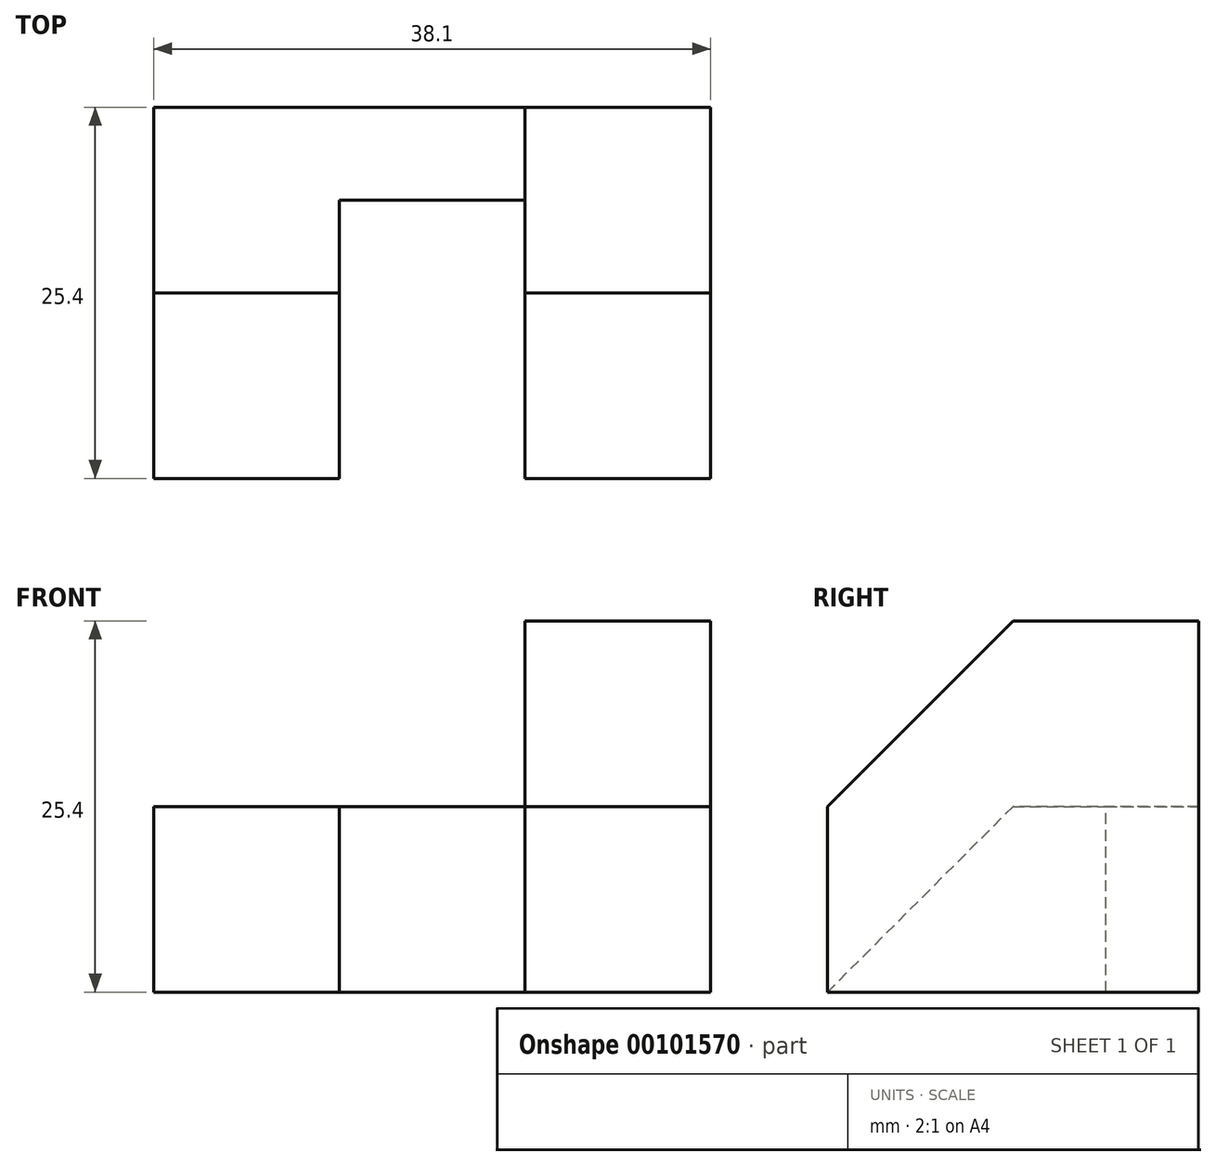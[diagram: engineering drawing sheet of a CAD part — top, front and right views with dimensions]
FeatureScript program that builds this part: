
annotation { "Feature Type Name" : "Feature", "Feature Type Description" : "" }
export const myFeature = defineFeature(function(context is Context, id is Id, definition is map)
    precondition{}
    {
        {
            var Q0;
            Q0=qCreatedBy(makeId("Right.planeOp"),FACE);
            var sketch = newSketch(context, id + "F0", { "sketchPlane" : qUnion([Q0])});
            skLineSegment(sketch, "E0.bottom", {"start": v(0, 0) * mm, "end": v(-25.4, 0) * mm});
            skLineSegment(sketch, "E0.top", {"start": v(0, -25.4) * mm, "end": v(-25.4, -25.4) * mm});
            skLineSegment(sketch, "E0.left", {"start": v(0, 0) * mm, "end": v(0, -25.4) * mm});
            skLineSegment(sketch, "E0.right", {"start": v(-25.4, 0) * mm, "end": v(-25.4, -25.4) * mm});
            skSolve(sketch);
        }
        {
            var Q0;
            Q0 = qSketchRegion(id + "F0", true);
            extrude(context, id + "F1", {"entities" : qUnion([Q0]), "endBound" : BoundingType.SYMMETRIC, "oppositeDirection" : true, "depth" : 38.1 * mm});
        }
        {
            var Q0;
            Q0=qCreatedBy(makeId("Top.planeOp"),FACE);
            var sketch = newSketch(context, id + "F2", { "sketchPlane" : qUnion([Q0])});
            skLineSegment(sketch, "E1.bottom", {"start": v(6.35, -25.4) * mm, "end": v(-6.35, -25.4) * mm});
            skLineSegment(sketch, "E1.top", {"start": v(6.35, -6.35) * mm, "end": v(-6.35, -6.35) * mm});
            skLineSegment(sketch, "E1.left", {"start": v(6.35, -25.4) * mm, "end": v(6.35, -6.35) * mm});
            skLineSegment(sketch, "E1.right", {"start": v(-6.35, -25.4) * mm, "end": v(-6.35, -6.35) * mm});
            skLineSegment(sketch, "E2", {"start": v(0, 0) * mm, "end": v(0, -25.4) * mm, "construction": true});
            skSolve(sketch);
        }
        {
            var Q0;
            Q0 = qSketchRegion(id + "F2", true);
            extrude(context, id + "F3", {"entities" : qUnion([Q0]), "operationType" : NewBodyOperationType.REMOVE, "endBound" : BoundingType.THROUGH_ALL, "oppositeDirection" : true, "depth" : 25.4 * mm});
        }
        {
            var Q0;
            Q0=qCreatedBy(makeId("Top.planeOp"),FACE);
            var sketch = newSketch(context, id + "F4", { "sketchPlane" : qUnion([Q0])});
            skLineSegment(sketch, "E3", {"start": v(6.35, -6.35) * mm, "end": v(6.35, 0) * mm});
            skLineSegment(sketch, "E4", {"start": v(6.35, 0) * mm, "end": v(-19.05, 0) * mm});
            skLineSegment(sketch, "E5", {"start": v(-19.05, 0) * mm, "end": v(-19.05, -25.4) * mm});
            skLineSegment(sketch, "E6", {"start": v(-19.05, -25.4) * mm, "end": v(-6.35, -25.4) * mm});
            skLineSegment(sketch, "E7", {"start": v(-6.35, -25.4) * mm, "end": v(-6.35, -6.35) * mm});
            skLineSegment(sketch, "E8", {"start": v(-6.35, -6.35) * mm, "end": v(6.35, -6.35) * mm});
            skSolve(sketch);
        }
        {
            var Q0;
            Q0 = qSketchRegion(id + "F4", true);
            extrude(context, id + "F5", {"entities" : qUnion([Q0]), "operationType" : NewBodyOperationType.REMOVE, "oppositeDirection" : true, "depth" : 12.7 * mm});
        }
        {
            var Q0;
            Q0=qCreatedBy(makeId("Right.planeOp"),FACE);
            var sketch = newSketch(context, id + "F6", { "sketchPlane" : qUnion([Q0])});
            skLineSegment(sketch, "E9", {"start": v(-12.7, -12.7) * mm, "end": v(-25.4, -25.4) * mm});
            skLineSegment(sketch, "E10", {"start": v(-25.4, -25.4) * mm, "end": v(-25.4, -12.7) * mm});
            skLineSegment(sketch, "E11", {"start": v(-25.4, -12.7) * mm, "end": v(-12.7, -12.7) * mm});
            skSolve(sketch);
        }
        {
            var Q0;
            Q0 = qSketchRegion(id + "F6", true);
            extrude(context, id + "F7", {"entities" : qUnion([Q0]), "operationType" : NewBodyOperationType.REMOVE, "endBound" : BoundingType.THROUGH_ALL, "oppositeDirection" : true, "depth" : 25.4 * mm});
        }
        {
            var Q0;
            Q0=qCreatedBy(makeId("Right.planeOp"),FACE);
            var sketch = newSketch(context, id + "F8", { "sketchPlane" : qUnion([Q0])});
            skLineSegment(sketch, "E12", {"start": v(-25.4, -12.7) * mm, "end": v(-25.4, 0) * mm});
            skLineSegment(sketch, "E13", {"start": v(-25.4, 0) * mm, "end": v(-12.7, 0) * mm});
            skLineSegment(sketch, "E14", {"start": v(-12.7, 0) * mm, "end": v(-25.4, -12.7) * mm});
            skSolve(sketch);
        }
        {
            var Q0;
            Q0 = qSketchRegion(id + "F8", true);
            extrude(context, id + "F9", {"entities" : qUnion([Q0]), "operationType" : NewBodyOperationType.REMOVE, "endBound" : BoundingType.THROUGH_ALL, "depth" : 25.4 * mm});
        }
    });
